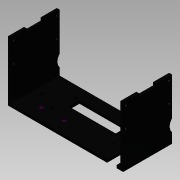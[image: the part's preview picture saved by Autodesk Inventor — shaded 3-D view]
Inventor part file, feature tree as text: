
AUTODESK INVENTOR PART (.ipt)
format: ipt  version: 2015 SP1 (Build 190203100, 203)  size: 209,920 bytes
history: native  units: mm
features: reference x18, extrude x10, sketch x9, plane x1
ambient origin geometry x8: Origin, YZ Plane, XZ Plane, XY Plane, X Axis, Y Axis, Z Axis, Center Point
bodies: Solid1 (feature_tree)
feature tree (38):
  sketch  "Sketch1"  dims[d0=120.812mm d1=51.214111mm]
  extrude  "Extrusion1"  Depth=51.214111mm
  extrude  "Extrusion2"  Depth=63.0mm TaperAngle=0.0deg
  plane  "Work Plane2"
  extrude  "Extrusion3"  Depth=3.0mm
  extrude  "Extrusion4"  [1 undecoded]
  extrude  "Extrusion5"  Depth=3.5mm
  extrude  "Extrusion7"  Depth=3.5mm
  extrude  "Extrusion8"  Depth=17.5mm
  extrude  "Extrusion9"  Depth=10.0mm TaperAngle=0.0deg
  extrude  "Extrusion11"  Depth=10.0mm TaperAngle=0.0deg
  extrude  "Extrusion12"  Depth=10.0mm
  sketch  "Sketch2"  dims[d4=3.0mm d5=0.0mm d6=63.0mm d7=0.0mm]
  reference  "Reference1"
  reference  "Reference2"
  reference  "Reference3"
  reference  "Reference4"
  sketch  "Sketch4"  dims[d8=3.0mm d9=3.0mm]
  sketch  "Sketch6"  dims[d10=114.812mm d11=-18.417445mm]
  reference  "Reference5"
  reference  "Reference6"
  sketch  "Sketch9"  dims[d12=3.5mm d13=3.5mm]
  reference  "Reference8"
  reference  "Reference9"
  reference  "Reference10"
  reference  "Reference11"
  sketch  "Sketch10"  dims[d14=3.5mm d15=3.5mm]
  sketch  "Sketch11"  dims[d16=10.0mm d17=0.0mm d18=17.5mm]
  reference  "Reference13"
  reference  "Reference14"
  reference  "Reference15"
  sketch  "Sketch15"  dims[d19=3.0mm d20=0.0mm d21=10.0mm d22=0.0mm]
  reference  "Reference21"
  sketch  "Sketch16"  dims[d25=200.0mm d26=0.0mm d29=10.0mm d30=0.0mm d31=3.5mm d32=3.5mm d33=2.0mm d34=2.0mm d35=10.0mm d36=0.0mm d37=2.0mm d38=2.0mm d39=90.0deg d47=10.0mm d48=0.0mm d49=10.0mm d50=17.5mm d51=10.0mm d52=0.0mm]
  reference  "Reference22"
  reference  "Reference23"
  reference  "Reference24"
  reference  "Reference25"
note: 1 required parameter value undecoded (feature->parameter linkage not recoverable at this tier; creation-order binding heuristic only, values carry confidence <= 0.55)
